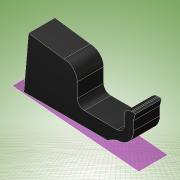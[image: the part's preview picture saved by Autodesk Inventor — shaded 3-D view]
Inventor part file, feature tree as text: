
AUTODESK INVENTOR PART (.ipt)
format: ipt  version: 2017 (Build 210142000, 142)  size: 155,648 bytes
history: native  units: in
note: dims shown in document units (in); Inventor stores cm internally (conversion verified against a paired STEP export)
features: extrude x2, sketch x2, plane x1
ambient origin geometry x8: Origin, YZ Plane, XZ Plane, XY Plane, X Axis, Y Axis, Z Axis, Center Point
bodies: Solid1 (feature_tree)
feature tree (5):
  extrude  "Extrusion1"  Depth=0.2in
  plane  "Work Plane1"
  extrude  "Extrusion2"  Depth=0.75in TaperAngle=0.0deg
  sketch  "Sketch1"  dims[d2=0.2in d3=0.2in]
  sketch  "Sketch2"  dims[d6=0.0344in d7=0.75in d8=0.0in d9=90.0deg d24=1.0in d25=0.0in d27=0.5in d28=0.2165in d29=0.2165in d30=0.0787in d31=0.0787in d32=0.0079in d33=1.0651in d34=1.0651in d35=0.125in]
